# Revit family: L&L_LUCE&LIGHT_PASITO_1.1
name_source: partatom
category: Lighting Fixtures
revit_build: Autodesk Revit 2018 (Build: 20181011_1500(x64)
units: mm (PartAtom-declared; Revit-internal decimal feet)

## family parameters
Always vertical = Yes
Cut with Voids When Loaded = No
Host = Wall
Light Source = Yes
OmniClass Number = 23.80.00.00
OmniClass Title = Electric Power and Lighting
Part Type = Normal
Room Calculation Point = No
Round Connector Dimension = Use Diameter
Shared = No

## types (2) — shared parameters
ACCESSORIES = outer casing for solid walls - https://www.lucelight.it
BIM BADGE = https://bim.archiproducts.com
BODY MATERIAL = ALUMINIUM
Color Filter = 16777215
Description = step light for outdoor applications; recessed (wall)
Dimming Lamp Color Temperature Shift = <None>
ENERGY EFFIECIENCY CLASS = A / A+ / A++
IES PHOTOMETRIC ARCHIVE = https://www.lucelight.it
LENGTH = 157 mm  [stored 0.515092 ft]
LIGHT MATERIAL = LIGHT_GLASS
Lamp = LED colour white: 2700K, 3000K, 4000K
MATERIAL DESCRIPTION = body in technopolymer and aluminium
Manufacturer = L&L Luce&Light
Model = PASITO 1.1
POWER CONSUMPTION = 10W (230Vac), 8.5W (24Vdc)
POWER SUPPLY = 230Vac, 24Vdc
PRODUCT CODE CONFIGURATOR = https://www.lucelight.it
PROTECTION LEVEL = IP 65
TECHNICAL SHEET = https://www.lucelight.it
THICKNESS = 43 mm  [stored 0.141076 ft]
Tilt Angle = 90.00°
Type Comments = recessed (wall)
URL = https://www.lucelight.it
URL CATALOGUE = https://www.lucelight.it
URL DESCRIPTION = https://www.lucelight.it
URL DXF = https://www.lucelight.it
URL IMAGE = https://www.lucelight.it
WEIGHT KG = 0.45
WIDTH = 143 mm

## per-type parameters (varying)
| type | Photometric Web File |
| PASITO_1.1 – Asymmetrical 150°x90° | PASITO 1.1 AT 150°x90° [2700K 8.5W 24Vdc] cor-ten.IES |
| PASITO_1.1 – 60° | PASITO 1.1 BE 60° [2700K 8.5W 24Vdc] white.IES |

note: [stored X ft] marks values corroborated as IEEE doubles in the binary element streams (Revit-internal decimal feet)

## geometry (parser evidence)
native form markers: Blend x2, Sweep x3
no freeform markers — native parametric forms only
